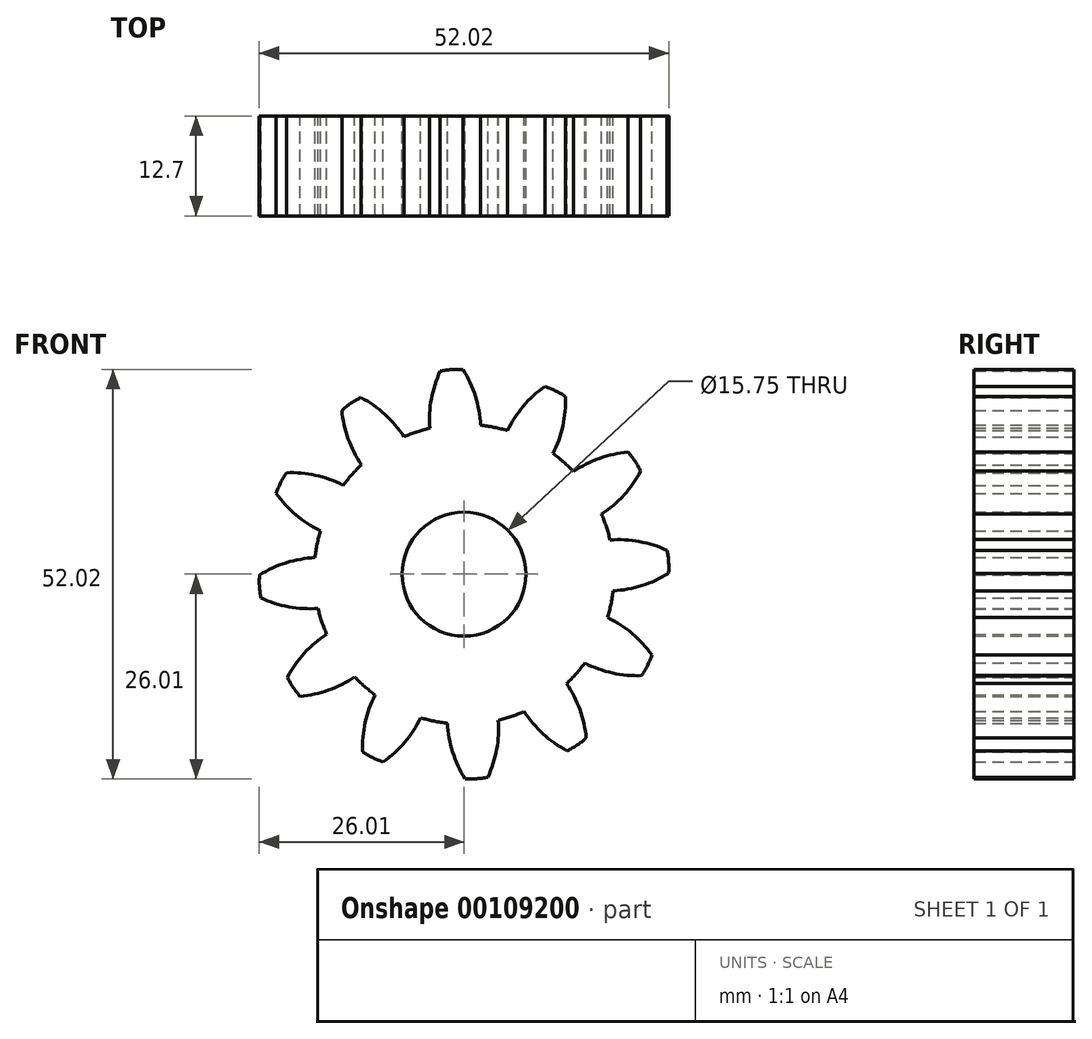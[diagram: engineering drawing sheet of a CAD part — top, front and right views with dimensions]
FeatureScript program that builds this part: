
annotation { "Feature Type Name" : "Feature", "Feature Type Description" : "" }
export const myFeature = defineFeature(function(context is Context, id is Id, definition is map)
    precondition{}
    {
        {
            var Q0;
            Q0=qCreatedBy(makeId("Front.planeOp"),FACE);
            var sketch = newSketch(context, id + "F0", { "sketchPlane" : qUnion([Q0])});
            skCircle(sketch, "E0", {"center": v(0, 0) * mm, "radius": 19.05 * mm});
            skLineSegment(sketch, "E1", {"start": v(0, 56.3) * mm, "end": v(0, -55.83) * mm, "construction": true});
            skArc(sketch, "E2", {"start": v(2.11, 18.93) * mm, "mid": v(1.45, 22.6) * mm, "end": v(-0.12, 25.98) * mm});
            skArc(sketch, "E3.MirrorCS", {"start": v(-4.34, 18.5) * mm, "mid": v(-4.15, 22.23) * mm, "end": v(-3.03, 25.79) * mm});
            skArc(sketch, "E4", {"start": v(-0.12, 25.98) * mm, "mid": v(-1.58, 25.99) * mm, "end": v(-3.03, 25.79) * mm});
            skCircle(sketch, "E5", {"center": v(0, 0) * mm, "radius": 7.87 * mm});
            skSolve(sketch);
        }
        {
            var Q0;
            Q0=makeQuery(id+"F0.imprint","IMPRINT",FACE,{"disambiguationData":[TD([[makeQuery(id+"F0.imprint","IMPRINT",EDGE,{"derivedFrom":sQuery(id+"F0.wireOp",EDGE,"E0")}),1.0]])]});
            var Q1;
            {var subQ0=sQuery(id+"F0.wireOp",EDGE,"E2");Q1=makeQuery(id+"F0.imprint","IMPRINT",FACE,{"disambiguationData":[TD([[makeQuery(id+"F0.imprint","IMPRINT",EDGE,{"derivedFrom":subQ0}),1.0]])]});}
            extrude(context, id + "F1", {"entities" : qUnion([Q0, Q1]), "depth" : 12.7 * mm});
        }
        {
            var Q0;
            Q0=makeQuery(id+"F1.opExtrude","SWEPT_BODY",BODY,{"disambiguationData":[OSD([sQuery(id+"F0.wireOp",EDGE,"E0"),sQuery(id+"F0.wireOp",EDGE,"E2"),sQuery(id+"F0.wireOp",EDGE,"E3.MirrorCS"),sQuery(id+"F0.wireOp",EDGE,"E4"),sQuery(id+"F0.wireOp",EDGE,"mQY0wwNy-6cYu-q0qe-OCgn-TzdDa7zRngHh")])]});
            var Q1;
            Q1=makeQuery(id+"F1.opExtrude","SWEPT_FACE",FACE,{"disambiguationData":[OSD([sQuery(id+"F0.wireOp",EDGE,"E0")])]});
            circularPattern(context, id + "F2", {"operationType" : NewBodyOperationType.ADD, "entities" : qUnion([Q0]), "axis" : qUnion([Q1]), "angle" : 30 * degree, "instanceCount" : 12});
        }
    });
